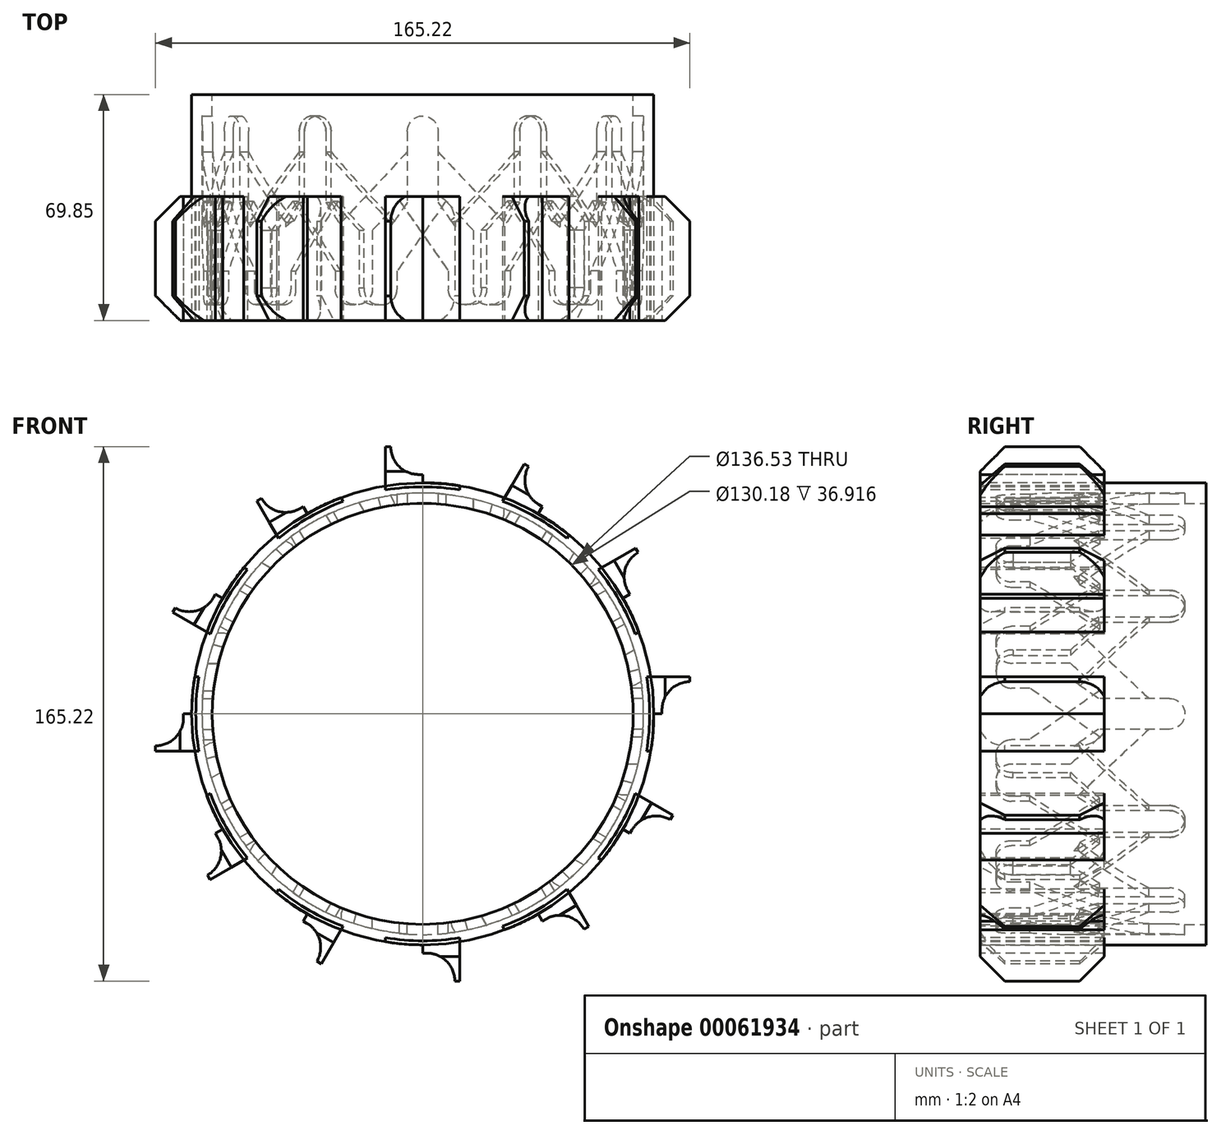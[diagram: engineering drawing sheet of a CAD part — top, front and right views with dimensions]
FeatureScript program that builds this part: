
annotation { "Feature Type Name" : "Feature", "Feature Type Description" : "" }
export const myFeature = defineFeature(function(context is Context, id is Id, definition is map)
    precondition{}
    {
        {
            var Q0;
            Q0=qCreatedBy(makeId("Front.planeOp"),FACE);
            var sketch = newSketch(context, id + "F0", { "sketchPlane" : qUnion([Q0])});
            skCircle(sketch, "E0", {"center": v(0, 0) * mm, "radius": 65.09 * mm});
            skCircle(sketch, "E1.0", {"center": v(0, 0) * mm, "radius": 71.44 * mm});
            skSolve(sketch);
        }
        {
            var Q0;
            Q0=makeQuery(id+"F0.imprint","IMPRINT",FACE,{"disambiguationData":[TD([[makeQuery(id+"F0.imprint","IMPRINT",EDGE,{"derivedFrom":sQuery(id+"F0.wireOp",EDGE,"E0")}),-1.0]])]});
            extrude(context, id + "F1", {"entities" : qUnion([Q0]), "depth" : 114.3 * mm});
        }
        {
            var Q0;
            Q0=qCreatedBy(makeId("Top.planeOp"),FACE);
            cPlane(context, id + "F2", {"entities" : qUnion([Q0]), "cplaneType" : CPlaneType.OFFSET, "offset" : 57.15 * mm, "width" : 152.4 * mm, "height" : 152.4 * mm});
        }
        {
            var Q0;
            Q0=qCreatedBy(id+"F2.planeOp",FACE);
            var sketch = newSketch(context, id + "F3", { "sketchPlane" : qUnion([Q0])});
            skArc(sketch, "E2", {"start": v(15.59, -104.16) * mm, "mid": v(20.13, -109.43) * mm, "end": v(25.08, -104.55) * mm});
            skLineSegment(sketch, "E3.0", {"start": v(4.76, -62.17) * mm, "end": v(25.08, -83.88) * mm});
            skLineSegment(sketch, "E4", {"start": v(25.08, -83.88) * mm, "end": v(25.08, -104.8) * mm});
            skLineSegment(sketch, "E5", {"start": v(4.76, -62.17) * mm, "end": v(4.76, -55.82) * mm});
            skArc(sketch, "E6", {"start": v(4.76, -55.82) * mm, "mid": v(0, -51.06) * mm, "end": v(-4.76, -55.82) * mm});
            skLineSegment(sketch, "E7", {"start": v(7.16, -77.38) * mm, "end": v(-7.94, -99) * mm});
            skLineSegment(sketch, "E8", {"start": v(-7.94, -99) * mm, "end": v(-7.94, -104.68) * mm});
            skLineSegment(sketch, "E9.0", {"start": v(-17.46, -96) * mm, "end": v(-17.46, -104.68) * mm});
            skArc(sketch, "E10", {"start": v(-17.46, -104.68) * mm, "mid": v(-12.7, -109.44) * mm, "end": v(-7.94, -104.68) * mm});
            skLineSegment(sketch, "E11.0", {"start": v(-4.76, -77.82) * mm, "end": v(-17.46, -96) * mm});
            skLineSegment(sketch, "E12.trimOffspring", {"start": v(7.16, -77.38) * mm, "end": v(15.59, -86.38) * mm});
            skPoint(sketch, "E13.orphan", {"position": v(-4.76, -65.66) * mm});
            skLineSegment(sketch, "E14.0", {"start": v(71.44, -114.3) * mm, "end": v(-71.44, -114.3) * mm});
            skLineSegment(sketch, "E15", {"start": v(15.59, -105.19) * mm, "end": v(15.59, -86.38) * mm});
            skLineSegment(sketch, "E16", {"start": v(-4.76, -77.82) * mm, "end": v(-4.76, -55.82) * mm});
            skSolve(sketch);
        }
        {
            var Q0;
            {var subQ7=sQuery(id+"F3.wireOp",EDGE,"E5");Q0=makeQuery(id+"F3.imprint","IMPRINT",FACE,{"disambiguationData":[TD([[makeQuery(id+"F3.imprint","IMPRINT",EDGE,{"derivedFrom":subQ7}),1.0]])]});}
            var Q1;
            {var subQ0=sQuery(id+"F3.wireOp",EDGE,"E10");var subQ1=makeQuery(id+"F3.imprint","INTERSECT",VERTEX,{"derivedFrom":[sQuery(id+"F3.wireOp",EDGE,"E8"),subQ0]});Q1=makeQuery(id+"F3.imprint","IMPRINT",FACE,{"disambiguationData":[TD([[makeQuery(id+"F3.imprint","IMPRINT",EDGE,{"disambiguationData":[TD([[subQ1,-1.0]])],"derivedFrom":subQ0}),1.0]])]});}
            var Q2;
            {var subQ0=sQuery(id+"F3.wireOp",EDGE,"E6");var subQ3=makeQuery(id+"F3.imprint","IMPRINT",VERTEX,{"derivedFrom":subQ0});Q2=makeQuery(id+"F3.imprint","IMPRINT",FACE,{"disambiguationData":[TD([[makeQuery(id+"F3.imprint","IMPRINT",EDGE,{"disambiguationData":[TD([[subQ3,1.0]])],"derivedFrom":subQ0}),1.0]])]});}
            var Q3;
            {var subQ1=sQuery(id+"F3.wireOp",EDGE,"E3.0");Q3=makeQuery(id+"F3.imprint","IMPRINT",FACE,{"disambiguationData":[TD([[makeQuery(id+"F3.imprint","IMPRINT",EDGE,{"derivedFrom":subQ1}),-1.0]])]});}
            var Q4;
            {var subQ0=sQuery(id+"F3.wireOp",EDGE,"E2");var subQ1=makeQuery(id+"F3.imprint","INTERSECT",VERTEX,{"derivedFrom":[subQ0,sQuery(id+"F3.wireOp",EDGE,"55f282a2-0efb-42c4-87fe-9c5e402fcb43.0")]});Q4=makeQuery(id+"F3.imprint","IMPRINT",FACE,{"disambiguationData":[TD([[makeQuery(id+"F3.imprint","IMPRINT",EDGE,{"disambiguationData":[TD([[subQ1,1.0]])],"derivedFrom":subQ0}),1.0]])]});}
            var Q5;
            {var subQ0=sQuery(id+"F3.wireOp",EDGE,"E6");var subQ1=makeQuery(id+"F3.imprint","INTERSECT",VERTEX,{"derivedFrom":[sQuery(id+"F3.wireOp",EDGE,"E5"),subQ0]});Q5=makeQuery(id+"F3.imprint","IMPRINT",FACE,{"disambiguationData":[TD([[makeQuery(id+"F3.imprint","IMPRINT",EDGE,{"disambiguationData":[TD([[subQ1,-1.0]])],"derivedFrom":subQ0}),1.0]])]});}
            extrude(context, id + "F4", {"entities" : qUnion([Q0, Q1, Q2, Q3, Q4, Q5]), "depth" : 19.05 * mm});
        }
        {
            var Q0;
            Q0=makeQuery(id+"F4.opExtrude","SWEPT_BODY",BODY,{"disambiguationData":[OSD([sQuery(id+"F3.wireOp",EDGE,"E2"),sQuery(id+"F3.wireOp",EDGE,"E3.0"),sQuery(id+"F3.wireOp",EDGE,"E4"),sQuery(id+"F3.wireOp",EDGE,"E5"),sQuery(id+"F3.wireOp",EDGE,"clDIjcJC-oWCI-1CYD-bKjD-LAr0MWrIur0Z"),sQuery(id+"F3.wireOp",EDGE,"E6"),sQuery(id+"F3.wireOp",EDGE,"55f282a2-0efb-42c4-87fe-9c5e402fcb43.0"),sQuery(id+"F3.wireOp",EDGE,"E7"),sQuery(id+"F3.wireOp",EDGE,"E8"),sQuery(id+"F3.wireOp",EDGE,"E9.0"),sQuery(id+"F3.wireOp",EDGE,"E10"),sQuery(id+"F3.wireOp",EDGE,"E11.0"),sQuery(id+"F3.wireOp",EDGE,"E12.trimOffspring")])]});
            var Q1;
            Q1=makeQuery(id+"F1.opExtrude","SWEPT_FACE",FACE,{"disambiguationData":[OSD([sQuery(id+"F0.wireOp",EDGE,"E0")])]});
            circularPattern(context, id + "F5", {"entities" : qUnion([Q0]), "axis" : qUnion([Q1]), "angle" : 30 * degree, "instanceCount" : round(12)});
        }
        {
            var Q0;
            Q0=makeQuery(id+"F5.opPattern","COPY",BODY,{"derivedFrom":makeQuery(id+"F4.opExtrude","SWEPT_BODY",BODY,{"disambiguationData":[OSD([sQuery(id+"F3.wireOp",EDGE,"E2"),sQuery(id+"F3.wireOp",EDGE,"E3.0"),sQuery(id+"F3.wireOp",EDGE,"E4"),sQuery(id+"F3.wireOp",EDGE,"E5"),sQuery(id+"F3.wireOp",EDGE,"clDIjcJC-oWCI-1CYD-bKjD-LAr0MWrIur0Z"),sQuery(id+"F3.wireOp",EDGE,"E6"),sQuery(id+"F3.wireOp",EDGE,"55f282a2-0efb-42c4-87fe-9c5e402fcb43.0"),sQuery(id+"F3.wireOp",EDGE,"E7"),sQuery(id+"F3.wireOp",EDGE,"E8"),sQuery(id+"F3.wireOp",EDGE,"E9.0"),sQuery(id+"F3.wireOp",EDGE,"E10"),sQuery(id+"F3.wireOp",EDGE,"E11.0"),sQuery(id+"F3.wireOp",EDGE,"E12.trimOffspring")])]}),"instanceName":"1"});
            var Q1;
            Q1=makeQuery(id+"F4.opExtrude","SWEPT_BODY",BODY,{"disambiguationData":[OSD([sQuery(id+"F3.wireOp",EDGE,"E2"),sQuery(id+"F3.wireOp",EDGE,"E3.0"),sQuery(id+"F3.wireOp",EDGE,"E4"),sQuery(id+"F3.wireOp",EDGE,"E5"),sQuery(id+"F3.wireOp",EDGE,"clDIjcJC-oWCI-1CYD-bKjD-LAr0MWrIur0Z"),sQuery(id+"F3.wireOp",EDGE,"E6"),sQuery(id+"F3.wireOp",EDGE,"55f282a2-0efb-42c4-87fe-9c5e402fcb43.0"),sQuery(id+"F3.wireOp",EDGE,"E7"),sQuery(id+"F3.wireOp",EDGE,"E8"),sQuery(id+"F3.wireOp",EDGE,"E9.0"),sQuery(id+"F3.wireOp",EDGE,"E10"),sQuery(id+"F3.wireOp",EDGE,"E11.0"),sQuery(id+"F3.wireOp",EDGE,"E12.trimOffspring")])]});
            var Q2;
            Q2=makeQuery(id+"F5.opPattern","COPY",BODY,{"derivedFrom":makeQuery(id+"F4.opExtrude","SWEPT_BODY",BODY,{"disambiguationData":[OSD([sQuery(id+"F3.wireOp",EDGE,"E2"),sQuery(id+"F3.wireOp",EDGE,"E3.0"),sQuery(id+"F3.wireOp",EDGE,"E4"),sQuery(id+"F3.wireOp",EDGE,"E5"),sQuery(id+"F3.wireOp",EDGE,"clDIjcJC-oWCI-1CYD-bKjD-LAr0MWrIur0Z"),sQuery(id+"F3.wireOp",EDGE,"E6"),sQuery(id+"F3.wireOp",EDGE,"55f282a2-0efb-42c4-87fe-9c5e402fcb43.0"),sQuery(id+"F3.wireOp",EDGE,"E7"),sQuery(id+"F3.wireOp",EDGE,"E8"),sQuery(id+"F3.wireOp",EDGE,"E9.0"),sQuery(id+"F3.wireOp",EDGE,"E10"),sQuery(id+"F3.wireOp",EDGE,"E11.0"),sQuery(id+"F3.wireOp",EDGE,"E12.trimOffspring")])]}),"instanceName":"9"});
            var Q3;
            Q3=makeQuery(id+"F5.opPattern","COPY",BODY,{"derivedFrom":makeQuery(id+"F4.opExtrude","SWEPT_BODY",BODY,{"disambiguationData":[OSD([sQuery(id+"F3.wireOp",EDGE,"E2"),sQuery(id+"F3.wireOp",EDGE,"E3.0"),sQuery(id+"F3.wireOp",EDGE,"E4"),sQuery(id+"F3.wireOp",EDGE,"E5"),sQuery(id+"F3.wireOp",EDGE,"clDIjcJC-oWCI-1CYD-bKjD-LAr0MWrIur0Z"),sQuery(id+"F3.wireOp",EDGE,"E6"),sQuery(id+"F3.wireOp",EDGE,"55f282a2-0efb-42c4-87fe-9c5e402fcb43.0"),sQuery(id+"F3.wireOp",EDGE,"E7"),sQuery(id+"F3.wireOp",EDGE,"E8"),sQuery(id+"F3.wireOp",EDGE,"E9.0"),sQuery(id+"F3.wireOp",EDGE,"E10"),sQuery(id+"F3.wireOp",EDGE,"E11.0"),sQuery(id+"F3.wireOp",EDGE,"E12.trimOffspring")])]}),"instanceName":"4"});
            var Q4;
            Q4=makeQuery(id+"F5.opPattern","COPY",BODY,{"derivedFrom":makeQuery(id+"F4.opExtrude","SWEPT_BODY",BODY,{"disambiguationData":[OSD([sQuery(id+"F3.wireOp",EDGE,"E2"),sQuery(id+"F3.wireOp",EDGE,"E3.0"),sQuery(id+"F3.wireOp",EDGE,"E4"),sQuery(id+"F3.wireOp",EDGE,"E5"),sQuery(id+"F3.wireOp",EDGE,"clDIjcJC-oWCI-1CYD-bKjD-LAr0MWrIur0Z"),sQuery(id+"F3.wireOp",EDGE,"E6"),sQuery(id+"F3.wireOp",EDGE,"55f282a2-0efb-42c4-87fe-9c5e402fcb43.0"),sQuery(id+"F3.wireOp",EDGE,"E7"),sQuery(id+"F3.wireOp",EDGE,"E8"),sQuery(id+"F3.wireOp",EDGE,"E9.0"),sQuery(id+"F3.wireOp",EDGE,"E10"),sQuery(id+"F3.wireOp",EDGE,"E11.0"),sQuery(id+"F3.wireOp",EDGE,"E12.trimOffspring")])]}),"instanceName":"3"});
            var Q5;
            Q5=makeQuery(id+"F5.opPattern","COPY",BODY,{"derivedFrom":makeQuery(id+"F4.opExtrude","SWEPT_BODY",BODY,{"disambiguationData":[OSD([sQuery(id+"F3.wireOp",EDGE,"E2"),sQuery(id+"F3.wireOp",EDGE,"E3.0"),sQuery(id+"F3.wireOp",EDGE,"E4"),sQuery(id+"F3.wireOp",EDGE,"E5"),sQuery(id+"F3.wireOp",EDGE,"clDIjcJC-oWCI-1CYD-bKjD-LAr0MWrIur0Z"),sQuery(id+"F3.wireOp",EDGE,"E6"),sQuery(id+"F3.wireOp",EDGE,"55f282a2-0efb-42c4-87fe-9c5e402fcb43.0"),sQuery(id+"F3.wireOp",EDGE,"E7"),sQuery(id+"F3.wireOp",EDGE,"E8"),sQuery(id+"F3.wireOp",EDGE,"E9.0"),sQuery(id+"F3.wireOp",EDGE,"E10"),sQuery(id+"F3.wireOp",EDGE,"E11.0"),sQuery(id+"F3.wireOp",EDGE,"E12.trimOffspring")])]}),"instanceName":"5"});
            var Q6;
            Q6=makeQuery(id+"F5.opPattern","COPY",BODY,{"derivedFrom":makeQuery(id+"F4.opExtrude","SWEPT_BODY",BODY,{"disambiguationData":[OSD([sQuery(id+"F3.wireOp",EDGE,"E2"),sQuery(id+"F3.wireOp",EDGE,"E3.0"),sQuery(id+"F3.wireOp",EDGE,"E4"),sQuery(id+"F3.wireOp",EDGE,"E5"),sQuery(id+"F3.wireOp",EDGE,"clDIjcJC-oWCI-1CYD-bKjD-LAr0MWrIur0Z"),sQuery(id+"F3.wireOp",EDGE,"E6"),sQuery(id+"F3.wireOp",EDGE,"55f282a2-0efb-42c4-87fe-9c5e402fcb43.0"),sQuery(id+"F3.wireOp",EDGE,"E7"),sQuery(id+"F3.wireOp",EDGE,"E8"),sQuery(id+"F3.wireOp",EDGE,"E9.0"),sQuery(id+"F3.wireOp",EDGE,"E10"),sQuery(id+"F3.wireOp",EDGE,"E11.0"),sQuery(id+"F3.wireOp",EDGE,"E12.trimOffspring")])]}),"instanceName":"6"});
            var Q7;
            Q7=makeQuery(id+"F5.opPattern","COPY",BODY,{"derivedFrom":makeQuery(id+"F4.opExtrude","SWEPT_BODY",BODY,{"disambiguationData":[OSD([sQuery(id+"F3.wireOp",EDGE,"E2"),sQuery(id+"F3.wireOp",EDGE,"E3.0"),sQuery(id+"F3.wireOp",EDGE,"E4"),sQuery(id+"F3.wireOp",EDGE,"E5"),sQuery(id+"F3.wireOp",EDGE,"clDIjcJC-oWCI-1CYD-bKjD-LAr0MWrIur0Z"),sQuery(id+"F3.wireOp",EDGE,"E6"),sQuery(id+"F3.wireOp",EDGE,"55f282a2-0efb-42c4-87fe-9c5e402fcb43.0"),sQuery(id+"F3.wireOp",EDGE,"E7"),sQuery(id+"F3.wireOp",EDGE,"E8"),sQuery(id+"F3.wireOp",EDGE,"E9.0"),sQuery(id+"F3.wireOp",EDGE,"E10"),sQuery(id+"F3.wireOp",EDGE,"E11.0"),sQuery(id+"F3.wireOp",EDGE,"E12.trimOffspring")])]}),"instanceName":"7"});
            var Q8;
            Q8=makeQuery(id+"F5.opPattern","COPY",BODY,{"derivedFrom":makeQuery(id+"F4.opExtrude","SWEPT_BODY",BODY,{"disambiguationData":[OSD([sQuery(id+"F3.wireOp",EDGE,"E2"),sQuery(id+"F3.wireOp",EDGE,"E3.0"),sQuery(id+"F3.wireOp",EDGE,"E4"),sQuery(id+"F3.wireOp",EDGE,"E5"),sQuery(id+"F3.wireOp",EDGE,"clDIjcJC-oWCI-1CYD-bKjD-LAr0MWrIur0Z"),sQuery(id+"F3.wireOp",EDGE,"E6"),sQuery(id+"F3.wireOp",EDGE,"55f282a2-0efb-42c4-87fe-9c5e402fcb43.0"),sQuery(id+"F3.wireOp",EDGE,"E7"),sQuery(id+"F3.wireOp",EDGE,"E8"),sQuery(id+"F3.wireOp",EDGE,"E9.0"),sQuery(id+"F3.wireOp",EDGE,"E10"),sQuery(id+"F3.wireOp",EDGE,"E11.0"),sQuery(id+"F3.wireOp",EDGE,"E12.trimOffspring")])]}),"instanceName":"8"});
            var Q9;
            Q9=makeQuery(id+"F5.opPattern","COPY",BODY,{"derivedFrom":makeQuery(id+"F4.opExtrude","SWEPT_BODY",BODY,{"disambiguationData":[OSD([sQuery(id+"F3.wireOp",EDGE,"E2"),sQuery(id+"F3.wireOp",EDGE,"E3.0"),sQuery(id+"F3.wireOp",EDGE,"E4"),sQuery(id+"F3.wireOp",EDGE,"E5"),sQuery(id+"F3.wireOp",EDGE,"clDIjcJC-oWCI-1CYD-bKjD-LAr0MWrIur0Z"),sQuery(id+"F3.wireOp",EDGE,"E6"),sQuery(id+"F3.wireOp",EDGE,"55f282a2-0efb-42c4-87fe-9c5e402fcb43.0"),sQuery(id+"F3.wireOp",EDGE,"E7"),sQuery(id+"F3.wireOp",EDGE,"E8"),sQuery(id+"F3.wireOp",EDGE,"E9.0"),sQuery(id+"F3.wireOp",EDGE,"E10"),sQuery(id+"F3.wireOp",EDGE,"E11.0"),sQuery(id+"F3.wireOp",EDGE,"E12.trimOffspring")])]}),"instanceName":"10"});
            var Q10;
            Q10=makeQuery(id+"F5.opPattern","COPY",BODY,{"derivedFrom":makeQuery(id+"F4.opExtrude","SWEPT_BODY",BODY,{"disambiguationData":[OSD([sQuery(id+"F3.wireOp",EDGE,"E2"),sQuery(id+"F3.wireOp",EDGE,"E3.0"),sQuery(id+"F3.wireOp",EDGE,"E4"),sQuery(id+"F3.wireOp",EDGE,"E5"),sQuery(id+"F3.wireOp",EDGE,"clDIjcJC-oWCI-1CYD-bKjD-LAr0MWrIur0Z"),sQuery(id+"F3.wireOp",EDGE,"E6"),sQuery(id+"F3.wireOp",EDGE,"55f282a2-0efb-42c4-87fe-9c5e402fcb43.0"),sQuery(id+"F3.wireOp",EDGE,"E7"),sQuery(id+"F3.wireOp",EDGE,"E8"),sQuery(id+"F3.wireOp",EDGE,"E9.0"),sQuery(id+"F3.wireOp",EDGE,"E10"),sQuery(id+"F3.wireOp",EDGE,"E11.0"),sQuery(id+"F3.wireOp",EDGE,"E12.trimOffspring")])]}),"instanceName":"11"});
            var Q11;
            Q11=makeQuery(id+"F5.opPattern","COPY",BODY,{"derivedFrom":makeQuery(id+"F4.opExtrude","SWEPT_BODY",BODY,{"disambiguationData":[OSD([sQuery(id+"F3.wireOp",EDGE,"E2"),sQuery(id+"F3.wireOp",EDGE,"E3.0"),sQuery(id+"F3.wireOp",EDGE,"E4"),sQuery(id+"F3.wireOp",EDGE,"E5"),sQuery(id+"F3.wireOp",EDGE,"clDIjcJC-oWCI-1CYD-bKjD-LAr0MWrIur0Z"),sQuery(id+"F3.wireOp",EDGE,"E6"),sQuery(id+"F3.wireOp",EDGE,"E7"),sQuery(id+"F3.wireOp",EDGE,"E8"),sQuery(id+"F3.wireOp",EDGE,"E9.0"),sQuery(id+"F3.wireOp",EDGE,"E10"),sQuery(id+"F3.wireOp",EDGE,"E11.0"),sQuery(id+"F3.wireOp",EDGE,"E12.trimOffspring"),sQuery(id+"F3.wireOp",EDGE,"E15")])]}),"instanceName":"2"});
            var Q12;
            Q12=makeQuery(id+"F1.opExtrude","SWEPT_BODY",BODY,{"disambiguationData":[OSD([sQuery(id+"F0.wireOp",EDGE,"E0"),sQuery(id+"F0.wireOp",EDGE,"E1.0")])]});
            booleanBodies(context, id + "F6", {"operationType" : BooleanOperationType.SUBTRACTION, "tools" : qUnion([Q0, Q1, Q2, Q3, Q4, Q5, Q6, Q7, Q8, Q9, Q10, Q11]), "targets" : qUnion([Q12])});
        }
        {
            var Q0;
            Q0=makeQuery(id+"F1.opExtrude","CAP_FACE",FACE,{"disambiguationData":[OSD([sQuery(id+"F0.wireOp",EDGE,"E0"),sQuery(id+"F0.wireOp",EDGE,"E1.0")])],"isStart":false});
            var sketch = newSketch(context, id + "F7", { "sketchPlane" : qUnion([Q0])});
            skCircle(sketch, "E17.0", {"center": v(0, 0) * mm, "radius": 71.44 * mm});
            skCircle(sketch, "E18.0", {"center": v(0, 0) * mm, "radius": 68.26 * mm});
            skSolve(sketch);
        }
        {
            var Q0;
            Q0=makeQuery(id+"F7.imprint","IMPRINT",FACE,{"disambiguationData":[TD([[makeQuery(id+"F7.imprint","IMPRINT",EDGE,{"derivedFrom":sQuery(id+"F7.wireOp",EDGE,"E17.0")}),1.0]])]});
            var Q1;
            Q1=makeQuery(id+"F1.opExtrude","CAP_FACE",FACE,{"disambiguationData":[OSD([sQuery(id+"F0.wireOp",EDGE,"E0"),sQuery(id+"F0.wireOp",EDGE,"E1.0")])],"isStart":true});
            extrude(context, id + "F8", {"entities" : qUnion([Q0]), "endBound" : BoundingType.UP_TO_SURFACE, "oppositeDirection" : true, "endBoundEntityFace" : qUnion([Q1]), "depth" : 25.4 * mm});
        }
        {
            var Q0;
            Q0=makeQuery(id+"F6.opBoolean","SPLIT",BODY,{"disambiguationData":[OD(0.0)],"derivedFrom":makeQuery(id+"F1.opExtrude","SWEPT_BODY",BODY,{"disambiguationData":[OSD([sQuery(id+"F0.wireOp",EDGE,"E0"),sQuery(id+"F0.wireOp",EDGE,"E1.0")])]})});
            var Q1;
            Q1=makeQuery(id+"F6.opBoolean","SPLIT",BODY,{"disambiguationData":[OD(1.0)],"derivedFrom":makeQuery(id+"F1.opExtrude","SWEPT_BODY",BODY,{"disambiguationData":[OSD([sQuery(id+"F0.wireOp",EDGE,"E0"),sQuery(id+"F0.wireOp",EDGE,"E1.0")])]})});
            var Q2;
            Q2=makeQuery(id+"F8.opExtrude","SWEPT_BODY",BODY,{"disambiguationData":[OSD([sQuery(id+"F7.wireOp",EDGE,"E17.0"),sQuery(id+"F7.wireOp",EDGE,"E18.0")])]});
            booleanBodies(context, id + "F9", {"operationType" : BooleanOperationType.UNION, "tools" : qUnion([Q0, Q1, Q2])});
        }
        {
            var Q0;
            Q0=makeQuery(id+"F1.opExtrude","CAP_FACE",FACE,{"disambiguationData":[OSD([sQuery(id+"F0.wireOp",EDGE,"E0"),sQuery(id+"F0.wireOp",EDGE,"E1.0")])],"isStart":true});
            extrude(context, id + "F10", {"entities" : qUnion([Q0]), "operationType" : NewBodyOperationType.REMOVE, "oppositeDirection" : true, "depth" : 44.45 * mm});
        }
        {
            var Q0;
            Q0=makeQuery(id+"F1.opExtrude","CAP_FACE",FACE,{"disambiguationData":[OSD([sQuery(id+"F0.wireOp",EDGE,"E0"),sQuery(id+"F0.wireOp",EDGE,"E1.0")])],"isStart":false});
            var sketch = newSketch(context, id + "F11", { "sketchPlane" : qUnion([Q0])});
            skLineSegment(sketch, "E19", {"start": v(9.9, 80.96) * mm, "end": v(9.9, 80.96) * mm});
            skLineSegment(sketch, "E20", {"start": v(11.5, 82.61) * mm, "end": v(11.5, 68.74) * mm});
            skLineSegment(sketch, "E21", {"start": v(0, 71.44) * mm, "end": v(0, 65.09) * mm});
            skLineSegment(sketch, "E22.MirrorCS", {"start": v(-11.5, 80.96) * mm, "end": v(-11.5, 68.83) * mm});
            skPoint(sketch, "E23.visualSharp", {"position": v(-9.9, 71.44) * mm});
            skPoint(sketch, "E24.visualSharp", {"position": v(9.9, 71.44) * mm});
            skCircle(sketch, "E25.0", {"center": v(0, 0) * mm, "radius": 71.44 * mm});
            skPoint(sketch, "E26.orphan", {"position": v(-11.5, 70.5) * mm});
            skPoint(sketch, "E27.orphan", {"position": v(11.5, 70.5) * mm});
            skLineSegment(sketch, "E28", {"start": v(11.5, 70.5) * mm, "end": v(11.5, 64.06) * mm});
            skLineSegment(sketch, "E29", {"start": v(-11.5, 70.5) * mm, "end": v(-11.5, 64.06) * mm});
            skCircle(sketch, "E30.0", {"center": v(0, 0) * mm, "radius": 70.17 * mm});
            skLineSegment(sketch, "E31", {"start": v(0, 71.44) * mm, "end": v(0, 73.98) * mm});
            skLineSegment(sketch, "E32", {"start": v(0, 73.98) * mm, "end": v(1.27, 73.98) * mm});
            skPoint(sketch, "E33.visualSharp", {"position": v(9.9, 73.98) * mm});
            skArc(sketch, "E33.filletArc", {"start": v(1.27, 73.98) * mm, "mid": v(7.38, 76.5) * mm, "end": v(9.9, 82.61) * mm});
            skLineSegment(sketch, "E34", {"start": v(9.9, 82.61) * mm, "end": v(11.5, 82.61) * mm});
            skPoint(sketch, "E35.orphan", {"position": v(11.5, 80.96) * mm});
            skLineSegment(sketch, "E36.MirrorCS", {"start": v(0, 73.98) * mm, "end": v(-1.27, 73.98) * mm});
            skArc(sketch, "E37.MirrorCS", {"start": v(-1.27, 73.98) * mm, "mid": v(-7.38, 76.5) * mm, "end": v(-9.9, 82.61) * mm});
            skLineSegment(sketch, "E38.MirrorCS", {"start": v(-9.9, 82.61) * mm, "end": v(-11.5, 82.61) * mm});
            skLineSegment(sketch, "E39.MirrorCS", {"start": v(-11.5, 82.61) * mm, "end": v(-11.5, 68.74) * mm});
            skSolve(sketch);
        }
        {
            var Q0;
            {var subQ1=sQuery(id+"F11.wireOp",EDGE,"Mt45pFoP-gQ0B-fhlW-3RWX-IFJhzfuhUNEr");Q0=makeQuery(id+"F11.imprint","IMPRINT",FACE,{"disambiguationData":[TD([[makeQuery(id+"F11.imprint","IMPRINT",EDGE,{"derivedFrom":subQ1}),-1.0]])]});}
            var Q1;
            {var subQ1=sQuery(id+"F11.wireOp",EDGE,"ba7c2c1e-1a2c-4f42-82b6-26c5c739176d0.MirrorCS");Q1=makeQuery(id+"F11.imprint","IMPRINT",FACE,{"disambiguationData":[TD([[makeQuery(id+"F11.imprint","IMPRINT",EDGE,{"derivedFrom":subQ1}),1.0]])]});}
            var Q2;
            {var subQ1=sQuery(id+"F11.wireOp",EDGE,"E21");var subQ3=sQuery(id+"F11.wireOp",EDGE,"E30.0");var subQ4=makeQuery(id+"F11.imprint","INTERSECT",VERTEX,{"derivedFrom":[subQ1,subQ3]});Q2=makeQuery(id+"F11.imprint","IMPRINT",FACE,{"disambiguationData":[TD([[makeQuery(id+"F11.imprint","IMPRINT",EDGE,{"disambiguationData":[TD([[subQ4,1.0]])],"derivedFrom":subQ3}),-1.0]])]});}
            var Q3;
            {var subQ1=sQuery(id+"F11.wireOp",EDGE,"E21");var subQ3=sQuery(id+"F11.wireOp",EDGE,"E30.0");var subQ4=makeQuery(id+"F11.imprint","INTERSECT",VERTEX,{"derivedFrom":[subQ1,subQ3]});Q3=makeQuery(id+"F11.imprint","IMPRINT",FACE,{"disambiguationData":[TD([[makeQuery(id+"F11.imprint","IMPRINT",EDGE,{"disambiguationData":[TD([[subQ4,-1.0]])],"derivedFrom":subQ3}),-1.0]])]});}
            var Q4;
            {var subQ2=sQuery(id+"F11.wireOp",EDGE,"E20");Q4=makeQuery(id+"F11.imprint","IMPRINT",FACE,{"disambiguationData":[TD([[makeQuery(id+"F11.imprint","IMPRINT",EDGE,{"derivedFrom":subQ2}),-1.0]])]});}
            var Q5;
            {var subQ0=sQuery(id+"F11.wireOp",EDGE,"E31");Q5=makeQuery(id+"F11.imprint","IMPRINT",FACE,{"disambiguationData":[TD([[makeQuery(id+"F11.imprint","IMPRINT",EDGE,{"derivedFrom":subQ0}),1.0]])]});}
            extrude(context, id + "F12", {"entities" : qUnion([Q0, Q1, Q2, Q3, Q4, Q5]), "oppositeDirection" : true, "depth" : 38.35 * mm});
        }
        {
            var Q0;
            Q0=makeQuery(id+"F12.opExtrude","CAP_EDGE",EDGE,{"disambiguationData":[OSD([sQuery(id+"F11.wireOp",EDGE,"E34")])],"isStart":true});
            var Q1;
            Q1=makeQuery(id+"F12.opExtrude","CAP_EDGE",EDGE,{"disambiguationData":[OSD([sQuery(id+"F11.wireOp",EDGE,"E38.MirrorCS")])],"isStart":true});
            var Q2;
            Q2=makeQuery(id+"F12.opExtrude","CAP_EDGE",EDGE,{"disambiguationData":[OSD([sQuery(id+"F11.wireOp",EDGE,"E38.MirrorCS")])],"isStart":false});
            var Q3;
            Q3=makeQuery(id+"F12.opExtrude","CAP_EDGE",EDGE,{"disambiguationData":[OSD([sQuery(id+"F11.wireOp",EDGE,"E34")])],"isStart":false});
            chamfer(context, id + "F13", {"entities" : qUnion([Q0, Q1, Q2, Q3]), "width" : 7.62 * mm, "tangentPropagation" : true});
        }
        {
            var Q0;
            Q0=makeQuery(id+"F12.opExtrude","SWEPT_BODY",BODY,{"disambiguationData":[OSD([sQuery(id+"F0.wireOp",EDGE,"E1.0"),sQuery(id+"F11.wireOp",EDGE,"ba7c2c1e-1a2c-4f42-82b6-26c5c739176d0.MirrorCS"),sQuery(id+"F11.wireOp",EDGE,"b90b369e-09d7-4cc0-b1ca-d99bbeda30b80.MirrorCS"),sQuery(id+"F11.wireOp",EDGE,"E22.MirrorCS"),sQuery(id+"F11.wireOp",EDGE,"E23.filletArc")])]});
            var Q1;
            Q1=makeQuery(id+"F12.opExtrude","SWEPT_BODY",BODY,{"disambiguationData":[OSD([sQuery(id+"F0.wireOp",EDGE,"E1.0"),sQuery(id+"F11.wireOp",EDGE,"Mt45pFoP-gQ0B-fhlW-3RWX-IFJhzfuhUNEr"),sQuery(id+"F11.wireOp",EDGE,"qRYB9R48-WzlS-g8gA-RO5B-KzFAviSElCBE"),sQuery(id+"F11.wireOp",EDGE,"E20"),sQuery(id+"F11.wireOp",EDGE,"E24.filletArc")])]});
            var Q2;
            {var subQ0=makeQuery(id+"F4.opExtrude","SWEPT_FACE",FACE,{"disambiguationData":[OSD([sQuery(id+"F3.wireOp",EDGE,"E2")])]});var subQ6=sQuery(id+"F0.wireOp",EDGE,"E1.0");var subQ8=makeQuery(id+"F1.opExtrude","SWEPT_FACE",FACE,{"disambiguationData":[OSD([subQ6])]});var subQ9=makeQuery(id+"F4.opExtrude","SWEPT_FACE",FACE,{"disambiguationData":[OSD([sQuery(id+"F3.wireOp",EDGE,"E3.0")])]});Q2=makeQuery(id+"F9.opBoolean","MERGE",FACE,{"derivedFrom":[makeQuery(id+"F6.opBoolean","SPLIT",FACE,{"disambiguationData":[TD([subQ9])],"derivedFrom":subQ8}),makeQuery(id+"F6.opBoolean","SPLIT",FACE,{"disambiguationData":[TD([subQ0])],"derivedFrom":subQ8}),makeQuery(id+"F8.opExtrude","SWEPT_FACE",FACE,{"disambiguationData":[OSD([sQuery(id+"F7.wireOp",EDGE,"E17.0")])]})]});}
            circularPattern(context, id + "F14", {"entities" : qUnion([Q0, Q1]), "axis" : qUnion([Q2]), "angle" : 30 * degree, "instanceCount" : 12});
        }
    });
